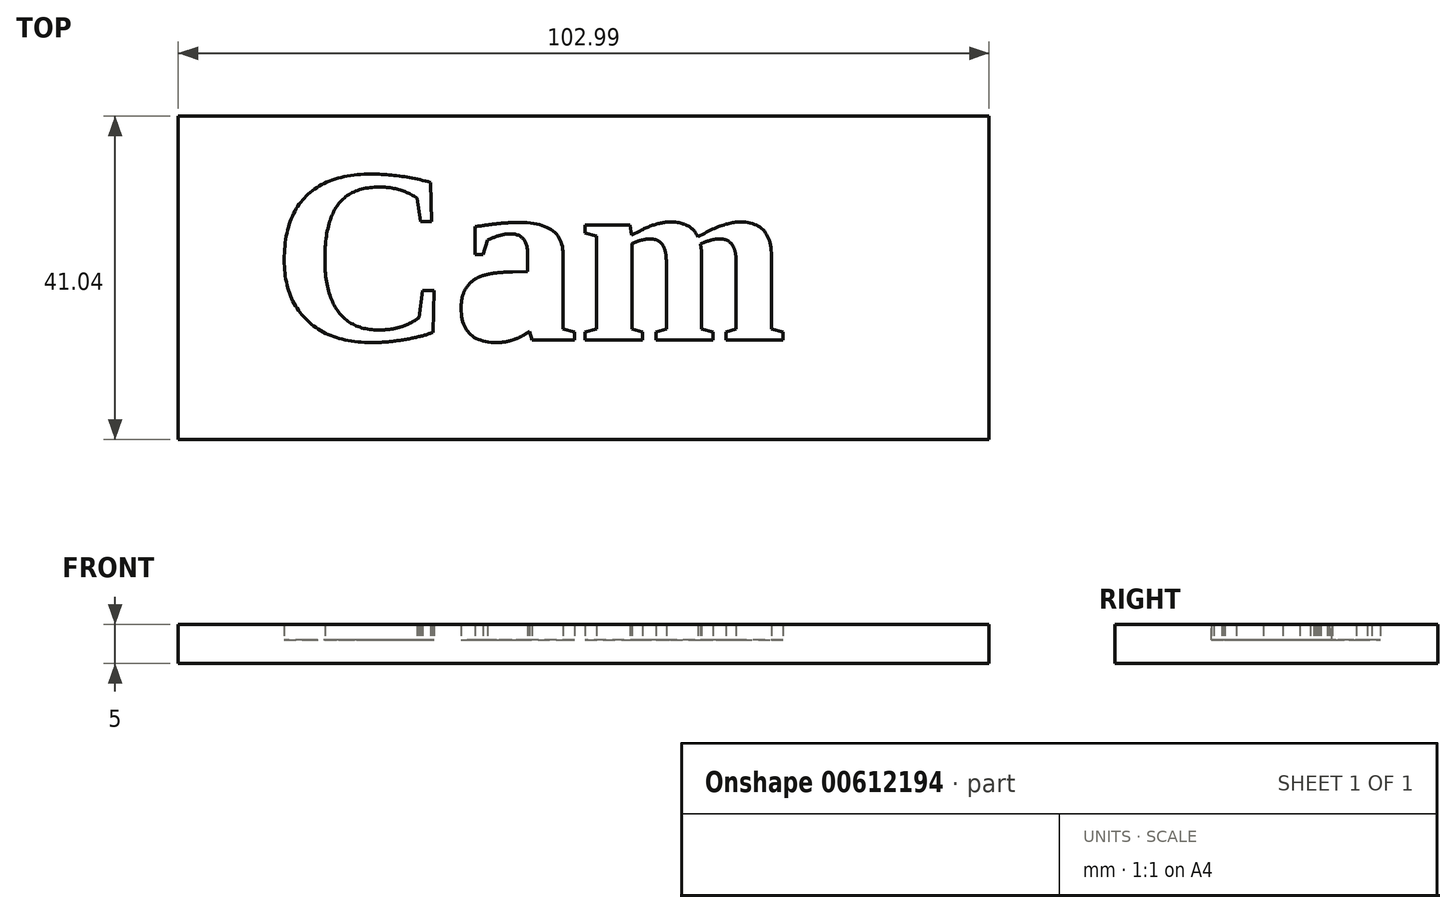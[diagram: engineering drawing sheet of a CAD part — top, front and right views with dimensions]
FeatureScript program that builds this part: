
annotation { "Feature Type Name" : "Feature", "Feature Type Description" : "" }
export const myFeature = defineFeature(function(context is Context, id is Id, definition is map)
    precondition{}
    {
        {
            var Q0;
            Q0=qCreatedBy(makeId("Top.planeOp"),FACE);
            var sketch = newSketch(context, id + "F0", { "sketchPlane" : qUnion([Q0])});
            skLineSegment(sketch, "E0.bottom", {"start": v(0, 0) * mm, "end": v(-102.99, 0) * mm});
            skLineSegment(sketch, "E0.top", {"start": v(0, -41.04) * mm, "end": v(-102.99, -41.04) * mm});
            skLineSegment(sketch, "E0.left", {"start": v(0, 0) * mm, "end": v(0, -41.04) * mm});
            skLineSegment(sketch, "E0.right", {"start": v(-102.99, 0) * mm, "end": v(-102.99, -41.04) * mm});
            skSolve(sketch);
        }
        {
            var Q0;
            Q0=makeQuery(id+"F0.imprint","IMPRINT",FACE,{"disambiguationData":[TD([[makeQuery(id+"F0.imprint","IMPRINT",EDGE,{"derivedFrom":sQuery(id+"F0.wireOp",EDGE,"E0.bottom")}),1.0]])]});
            extrude(context, id + "F1", {"entities" : qUnion([Q0]), "depth" : 3 * mm, "offsetDistance" : 25 * mm});
        }
        {
            var Q0;
            Q0=makeQuery(id+"F1.opExtrude","CAP_FACE",FACE,{"disambiguationData":[OSD([sQuery(id+"F0.wireOp",EDGE,"E0.bottom"),sQuery(id+"F0.wireOp",EDGE,"E0.top"),sQuery(id+"F0.wireOp",EDGE,"E0.left"),sQuery(id+"F0.wireOp",EDGE,"E0.right")])],"isStart":false});
            var sketch = newSketch(context, id + "F2", { "sketchPlane" : qUnion([Q0])});
            skText(sketch, "E1", { "text": "Cam", "fontName": "Tinos-Bold.ttf"});
            const initialGuessF2  = {"E1": [-0.09108, -0.02844, 1, 0, 0.02293]};
            skSetInitialGuess(sketch, initialGuessF2);
            skSolve(sketch);
        }
        {
            var Q0;
            Q0=makeQuery(id+"F2.imprint","IMPRINT",FACE,{"disambiguationData":[TD([[makeQuery(id+"F2.imprint","IMPRINT",EDGE,{"derivedFrom":sQuery(id+"F2.wireOp",EDGE,"E1.sketch_text.stroke-0")}),1.0]])]});
            extrude(context, id + "F3", {"entities" : qUnion([Q0]), "operationType" : NewBodyOperationType.ADD, "depth" : 2 * mm, "offsetDistance" : 25 * mm});
        }
    });
